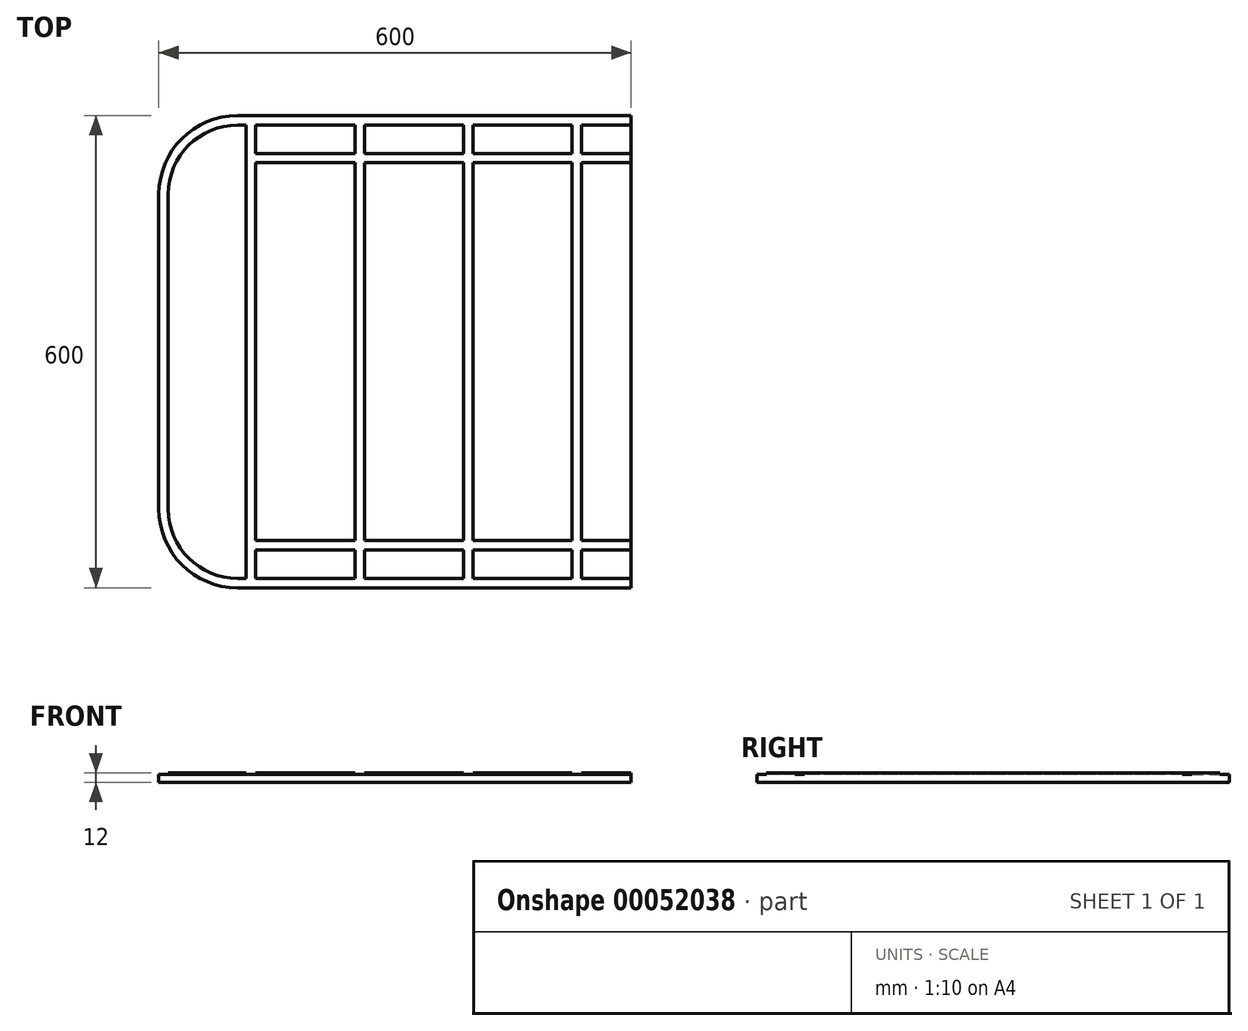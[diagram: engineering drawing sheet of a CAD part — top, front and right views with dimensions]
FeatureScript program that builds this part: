
annotation { "Feature Type Name" : "Feature", "Feature Type Description" : "" }
export const myFeature = defineFeature(function(context is Context, id is Id, definition is map)
    precondition{}
    {
        {
            var Q0;
            Q0=qCreatedBy(makeId("Top.planeOp"),FACE);
            var sketch = newSketch(context, id + "F0", { "sketchPlane" : qUnion([Q0])});
            skLineSegment(sketch, "E0.rect.bottom", {"start": v(300, 300) * mm, "end": v(-300, 300) * mm, "construction": true});
            skLineSegment(sketch, "E0.rect.top", {"start": v(300, -300) * mm, "end": v(-300, -300) * mm, "construction": true});
            skLineSegment(sketch, "E0.rect.left", {"start": v(300, 300) * mm, "end": v(300, -300) * mm, "construction": true});
            skLineSegment(sketch, "E0.rect.right", {"start": v(-300, 300) * mm, "end": v(-300, -300) * mm, "construction": true});
            skPoint(sketch, "E0.rect.middle", {"position": v(0, 0) * mm});
            skLineSegment(sketch, "E1", {"start": v(300, 300) * mm, "end": v(-200, 300) * mm});
            skLineSegment(sketch, "E2", {"start": v(-200, -300) * mm, "end": v(300, -300) * mm});
            skLineSegment(sketch, "E3", {"start": v(-300, 200) * mm, "end": v(-300, -200) * mm});
            skPoint(sketch, "E4.visualSharp", {"position": v(-300, 300) * mm});
            skArc(sketch, "E4.filletArc", {"start": v(-200, 300) * mm, "mid": v(-270.71, 270.71) * mm, "end": v(-300, 200) * mm});
            skPoint(sketch, "E5.visualSharp", {"position": v(-300, -300) * mm});
            skArc(sketch, "E5.filletArc", {"start": v(-300, -200) * mm, "mid": v(-270.71, -270.71) * mm, "end": v(-200, -300) * mm});
            skLineSegment(sketch, "E6.0", {"start": v(-200, -288) * mm, "end": v(300, -288) * mm});
            skLineSegment(sketch, "E6.1", {"start": v(300, 288) * mm, "end": v(-200, 288) * mm});
            skArc(sketch, "E6.2", {"start": v(-200, 288) * mm, "mid": v(-262.23, 262.23) * mm, "end": v(-288, 200) * mm});
            skLineSegment(sketch, "E6.3", {"start": v(-288, 200) * mm, "end": v(-288, -200) * mm});
            skArc(sketch, "E6.4", {"start": v(-288, -200) * mm, "mid": v(-262.23, -262.23) * mm, "end": v(-200, -288) * mm});
            skLineSegment(sketch, "E7", {"start": v(300, 300) * mm, "end": v(300, -300) * mm});
            skSolve(sketch);
        }
        {
            var Q0;
            Q0=qSketchRegion(id+"F0",true);
            extrude(context, id + "F1", {"entities" : qUnion([Q0]), "oppositeDirection" : true, "depth" : 10 * mm});
        }
        {
            var Q0;
            Q0=qCreatedBy(makeId("Top.planeOp"),FACE);
            var sketch = newSketch(context, id + "F2", { "sketchPlane" : qUnion([Q0])});
            skLineSegment(sketch, "E8.0", {"start": v(300, 300) * mm, "end": v(-300, 300) * mm, "construction": true});
            skLineSegment(sketch, "E8.1", {"start": v(300, -300) * mm, "end": v(-300, -300) * mm, "construction": true});
            skLineSegment(sketch, "E8.2", {"start": v(300, 300) * mm, "end": v(300, -240) * mm});
            skLineSegment(sketch, "E8.3", {"start": v(-300, 300) * mm, "end": v(-300, -300) * mm, "construction": true});
            skPoint(sketch, "E8.4", {"position": v(0, 0) * mm});
            skPoint(sketch, "E8.8", {"position": v(-300, 300) * mm});
            skPoint(sketch, "E8.10", {"position": v(-300, -300) * mm});
            skLineSegment(sketch, "E8.12", {"start": v(-200, -288) * mm, "end": v(-189, -288) * mm});
            skLineSegment(sketch, "E8.13", {"start": v(300, 288) * mm, "end": v(237, 288) * mm});
            skArc(sketch, "E8.14", {"start": v(-200, 288) * mm, "mid": v(-262.23, 262.23) * mm, "end": v(-288, 200) * mm});
            skLineSegment(sketch, "E8.15", {"start": v(-288, 200) * mm, "end": v(-288, -200) * mm});
            skArc(sketch, "E8.16", {"start": v(-288, -200) * mm, "mid": v(-262.23, -262.23) * mm, "end": v(-200, -288) * mm});
            skLineSegment(sketch, "E8.17", {"start": v(300, 300) * mm, "end": v(300, 252) * mm});
            skLineSegment(sketch, "E9", {"start": v(-177, 252) * mm, "end": v(-51, 252) * mm});
            skLineSegment(sketch, "E10", {"start": v(-39, 252) * mm, "end": v(87, 252) * mm});
            skLineSegment(sketch, "E11", {"start": v(99, 252) * mm, "end": v(225, 252) * mm});
            skLineSegment(sketch, "E12", {"start": v(-189, 252) * mm, "end": v(-189, -288) * mm});
            skLineSegment(sketch, "E13", {"start": v(237, 240) * mm, "end": v(237, -240) * mm});
            skLineSegment(sketch, "E14", {"start": v(-177, -288) * mm, "end": v(-177, -252) * mm});
            skLineSegment(sketch, "E15", {"start": v(-177, 240) * mm, "end": v(-51, 240) * mm});
            skLineSegment(sketch, "E16", {"start": v(-51, 240) * mm, "end": v(-51, -240) * mm});
            skLineSegment(sketch, "E17", {"start": v(-39, 240) * mm, "end": v(-39, -240) * mm});
            skLineSegment(sketch, "E18", {"start": v(-39, 240) * mm, "end": v(87, 240) * mm});
            skLineSegment(sketch, "E19", {"start": v(87, 240) * mm, "end": v(87, -240) * mm});
            skLineSegment(sketch, "E20", {"start": v(99, -288) * mm, "end": v(99, -252) * mm});
            skLineSegment(sketch, "E21", {"start": v(99, 240) * mm, "end": v(225, 240) * mm});
            skLineSegment(sketch, "E22", {"start": v(225, 240) * mm, "end": v(225, -240) * mm});
            skLineSegment(sketch, "E23", {"start": v(300, 0) * mm, "end": v(-300, 0) * mm, "construction": true});
            skLineSegment(sketch, "E24.MirrorCS", {"start": v(-177, -252) * mm, "end": v(-51, -252) * mm});
            skLineSegment(sketch, "E25.MirrorCS", {"start": v(-39, -240) * mm, "end": v(87, -240) * mm});
            skLineSegment(sketch, "E26.MirrorCS", {"start": v(-177, -240) * mm, "end": v(-51, -240) * mm});
            skLineSegment(sketch, "E27.MirrorCS", {"start": v(99, -240) * mm, "end": v(225, -240) * mm});
            skLineSegment(sketch, "E28.MirrorCS", {"start": v(-39, -252) * mm, "end": v(87, -252) * mm});
            skLineSegment(sketch, "E29.MirrorCS", {"start": v(99, -252) * mm, "end": v(225, -252) * mm});
            skLineSegment(sketch, "E30", {"start": v(-189, 252) * mm, "end": v(-189, 288) * mm});
            skLineSegment(sketch, "E31", {"start": v(-177, 252) * mm, "end": v(-177, 288) * mm});
            skLineSegment(sketch, "E32", {"start": v(-51, 252) * mm, "end": v(-51, 288) * mm});
            skLineSegment(sketch, "E33", {"start": v(-39, 252) * mm, "end": v(-39, 288) * mm});
            skLineSegment(sketch, "E34", {"start": v(87, 252) * mm, "end": v(87, 288) * mm});
            skLineSegment(sketch, "E35", {"start": v(99, 252) * mm, "end": v(99, 288) * mm});
            skLineSegment(sketch, "E36", {"start": v(225, 252) * mm, "end": v(225, 288) * mm});
            skLineSegment(sketch, "E37", {"start": v(237, 252) * mm, "end": v(237, 288) * mm});
            skLineSegment(sketch, "E38.trimOffspring", {"start": v(-51, 288) * mm, "end": v(-177, 288) * mm});
            skLineSegment(sketch, "E39.trimOffspring", {"start": v(87, 288) * mm, "end": v(-39, 288) * mm});
            skLineSegment(sketch, "E40.trimOffspring", {"start": v(225, 288) * mm, "end": v(99, 288) * mm});
            skLineSegment(sketch, "E41.trimOffspring", {"start": v(-189, 288) * mm, "end": v(-200, 288) * mm});
            skLineSegment(sketch, "E42.trimOffspring", {"start": v(237, -288) * mm, "end": v(300, -288) * mm});
            skPoint(sketch, "E43.MirrorCS.end.orphan", {"position": v(237, -252) * mm});
            skLineSegment(sketch, "E44.trimOffspring", {"start": v(225, -252) * mm, "end": v(225, -288) * mm});
            skLineSegment(sketch, "E45.trimOffspring", {"start": v(99, -240) * mm, "end": v(99, 240) * mm});
            skLineSegment(sketch, "E46.trimOffspring", {"start": v(87, -252) * mm, "end": v(87, -288) * mm});
            skLineSegment(sketch, "E47.trimOffspring", {"start": v(-39, -252) * mm, "end": v(-39, -288) * mm});
            skLineSegment(sketch, "E48.trimOffspring", {"start": v(-51, -252) * mm, "end": v(-51, -288) * mm});
            skLineSegment(sketch, "E49.trimOffspring", {"start": v(-177, -240) * mm, "end": v(-177, 240) * mm});
            skPoint(sketch, "E50.MirrorCS.start.orphan", {"position": v(-189, -252) * mm});
            skLineSegment(sketch, "E51.trimOffspring", {"start": v(-177, -288) * mm, "end": v(-51, -288) * mm});
            skLineSegment(sketch, "E52.trimOffspring", {"start": v(-39, -288) * mm, "end": v(87, -288) * mm});
            skLineSegment(sketch, "E53.trimOffspring", {"start": v(99, -288) * mm, "end": v(225, -288) * mm});
            skPoint(sketch, "E8.6.start.orphan", {"position": v(-200, -300) * mm});
            skPoint(sketch, "E8.11.end.orphan", {"position": v(-200, -300) * mm});
            skPoint(sketch, "E8.11.start.orphan", {"position": v(-300, -200) * mm});
            skPoint(sketch, "E8.7.start.orphan", {"position": v(-300, 200) * mm});
            skPoint(sketch, "E8.9.end.orphan", {"position": v(-300, 200) * mm});
            skPoint(sketch, "E8.9.start.orphan", {"position": v(-200, 300) * mm});
            skPoint(sketch, "E8.5.end.orphan", {"position": v(-200, 300) * mm});
            skPoint(sketch, "E8.5.start.orphan", {"position": v(300, 300) * mm});
            skPoint(sketch, "E54.trimOffspring.start.orphan", {"position": v(-177, -300) * mm});
            skPoint(sketch, "E55.trimOffspring.end.orphan", {"position": v(300, -300) * mm});
            skLineSegment(sketch, "E56", {"start": v(237, 252) * mm, "end": v(300, 252) * mm});
            skLineSegment(sketch, "E57", {"start": v(237, 240) * mm, "end": v(300, 240) * mm});
            skLineSegment(sketch, "E58.trimOffspring", {"start": v(300, 240) * mm, "end": v(300, -288) * mm});
            skLineSegment(sketch, "E59", {"start": v(237, -240) * mm, "end": v(300, -240) * mm});
            skLineSegment(sketch, "E60", {"start": v(237, -252) * mm, "end": v(300, -252) * mm});
            skLineSegment(sketch, "E61.trimOffspring", {"start": v(237, -252) * mm, "end": v(237, -288) * mm});
            skLineSegment(sketch, "E62.trimOffspring", {"start": v(300, -252) * mm, "end": v(300, -288) * mm});
            skLineSegment(sketch, "E63", {"start": v(237, 240) * mm, "end": v(225, 240) * mm, "construction": true});
            skLineSegment(sketch, "E64", {"start": v(99, 240) * mm, "end": v(87, 240) * mm, "construction": true});
            skLineSegment(sketch, "E65", {"start": v(-39, 240) * mm, "end": v(-51, 240) * mm, "construction": true});
            skLineSegment(sketch, "E66", {"start": v(-177, 240) * mm, "end": v(-189, 240) * mm, "construction": true});
            skSolve(sketch);
        }
        {
            var Q0;
            Q0=qSketchRegion(id+"F2",true);
            extrude(context, id + "F3", {"entities" : qUnion([Q0]), "operationType" : NewBodyOperationType.ADD, "depth" : 2 * mm});
        }
    });
